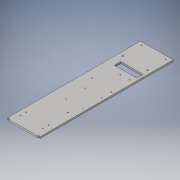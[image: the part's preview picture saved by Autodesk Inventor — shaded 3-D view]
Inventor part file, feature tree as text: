
AUTODESK INVENTOR PART (.ipt)
format: ipt  version: 2016 (Build 200138000, 138)  size: 267,776 bytes
history: native  units: in
note: dims shown in document units (in); Inventor stores cm internally (conversion verified against a paired STEP export)
features: extrude x12, sketch x12
ambient origin geometry x8: Origin, YZ Plane, XZ Plane, XY Plane, X Axis, Y Axis, Z Axis, Center Point
bodies: Solid1 (feature_tree)
feature tree (24):
  extrude  "Extrusion1"  Depth=3.94in
  extrude  "Extrusion3"  Depth=0.213in
  extrude  "Extrusion4"  Depth=2.9in
  extrude  "Extrusion5"  Depth=1.0in TaperAngle=0.0deg
  extrude  "Extrusion6"  Depth=0.25in
  extrude  "Extrusion7"  Depth=0.25in TaperAngle=0.0deg
  extrude  "Extrusion8"  Depth=0.1181in
  extrude  "Extrusion9"  Depth=2.147in TaperAngle=0.0deg
  extrude  "Extrusion10"  Depth=3.0in
  extrude  "Extrusion11"  Depth=0.477in
  extrude  "Extrusion12"  Depth=0.935in
  extrude  "Extrusion13"  Depth=0.3in
  sketch  "Sketch1"  dims[d0=3.94in d1=14.0in]
  sketch  "Sketch5"  dims[d2=0.213in d3=0.0in d8=0.1181in]
  sketch  "Sketch6"  dims[d9=0.1181in d10=2.9in]
  sketch  "Sketch7"  dims[d11=0.379in d12=1.0in d13=0.0in]
  sketch  "Sketch8"  dims[d14=0.11in d15=0.25in]
  sketch  "Sketch9"  dims[d16=0.25in d17=1.0in d18=0.0in]
  sketch  "Sketch10"  dims[d19=0.1181in d20=0.1181in]
  sketch  "Sketch11"  dims[d21=10.0in d22=0.0in d23=2.147in d24=0.0in]
  sketch  "Sketch12"  dims[d25=2.147in d26=0.0in d27=3.0in]
  sketch  "Sketch13"  dims[d28=1.0in d29=0.477in]
  sketch  "Sketch14"  dims[d30=0.463in d31=0.935in]
  sketch  "Sketch15"  dims[d32=0.3in d33=0.3in d34=1.0in d35=1.0in d36=2.7in d37=0.7in d38=0.7in d39=2.7in d40=0.1181in d41=0.1181in d42=0.1181in d43=0.1181in d44=0.15in d45=1.0in d46=1.0in d47=0.3in d48=0.3in d49=0.3in d50=0.3in d51=3.0in d52=1.0in d53=1.0in d54=0.7in d55=2.147in d56=0.0in d57=5.579in d58=0.323in d59=0.086in d60=0.086in d62=2.036in d63=2.281in d64=2.281in d65=2.147in d66=0.0in d67=0.121in d68=0.341in d69=8.925in d75=1.0in d76=0.0in d89=0.599in d90=0.104in d91=2.958in d92=2.103in d93=0.08in d94=0.116in d95=1.472in d96=0.55in d97=2.958in d98=0.121in d99=0.104in d100=0.121in d101=0.104in d102=1.098in d103=0.297in d104=2.3788in d105=1.0in d106=0.0in d107=3.3244in d108=0.429in d109=0.5in d110=0.084in d111=0.084in d114=0.274in d115=1.0in d116=0.0in d117=0.1181in d119=4.148in d120=0.85in d121=0.1181in d122=0.941in d123=9.225in d124=1.0in d125=0.0in]
